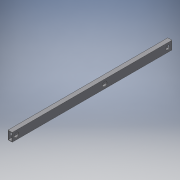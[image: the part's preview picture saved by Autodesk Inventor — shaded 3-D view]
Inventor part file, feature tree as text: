
AUTODESK INVENTOR PART (.ipt)
format: ipt  version: 2018 (Build 220112000, 112)  size: 139,776 bytes
history: native  units: in
note: dims shown in document units (in); Inventor stores cm internally (conversion verified against a paired STEP export)
features: extrude x5, sketch x5
ambient origin geometry x8: Origin, YZ Plane, XZ Plane, XY Plane, X Axis, Y Axis, Z Axis, Center Point
bodies: Solid1 (feature_tree)
feature tree (10):
  extrude  "Extrusion1"  Depth=2.0in
  extrude  "Extrusion2"  Depth=38.0in TaperAngle=0.0deg
  extrude  "Extrusion3"  Depth=1.0in TaperAngle=0.0deg
  extrude  "Extrusion4"  Depth=1.0in
  extrude  "Extrusion5"  Depth=1.0in TaperAngle=0.0deg
  sketch  "Sketch1"  dims[d0=1.0in d1=2.0in]
  sketch  "Sketch2"  dims[d2=0.125in d3=38.0in d4=0.0in]
  sketch  "Sketch3"  dims[d5=1.0in d7=10.0in d8=0.0in]
  sketch  "Sketch4"  dims[d9=1.0in d10=1.0in]
  sketch  "Sketch5"  dims[d11=1.125in d12=1.0in d13=0.0in d14=22.0in d15=1.125in d16=1.0in d17=0.0in d18=1.0in d19=135.0deg d20=1.0in d21=0.16in d22=0.16in d23=1.0in d24=0.0in]
